# Revit family: QF_BOURGEAT_Satellite4GT_froid_2-1_porte_pleine
name_source: partatom
category: Equipement spécialisé
revit_build: Autodesk Revit 2015 (Build: 20140606_1530(x64)
units: mm (PartAtom-declared; Revit-internal decimal feet)

## types (2) — shared parameters
Certification = NF hygiene alimentaire
Charge max = 300.00 kg
Charge_gaz = 0.220 Kg
Classe Climatique = 4
Consommation énergétique = 4.3Kw/h NFD40-016
Diametre_roue = 160 mm  [stored 0.524934 ft]
Fabricant = BOURGEAT
Fréquence = 50 Hz
Hauteur hors tout = 1876 mm
Hauteur_poignee_porte_sol = 816 mm
Hauteur_poignees_laterales = 905 mm  [stored 2.96916 ft]
Hauteur_porte = 1629 mm  [stored 5.34449 ft]
Hauteur_roue = 200 mm  [stored 0.656168 ft]
Indice de protection = IP25
Intensité nominale = 2 A
Largeur_porte = 706 mm  [stored 2.31627 ft]
Longueur hors tout = 791 mm
Longueur_poignees_laterales = 973 mm  [stored 3.19226 ft]
Materiau_Poignee_porte = B_Elastomère_TPE_S
Materiau_bac = B_Elastomère_TPE_S
Materiau_bandage = B_Elastomère_TPE_S
Materiau_porte = Acier inoxydable, brossé
Materiau_vitre = Verre, vitrage transparent, trempé
Nature isolant = Mousse sans PU
Phase = 2
Poids net à vide = 160.00 kg
Pos_V_IHM = 197 mm
Profondeur hors tout = 1129 mm  [stored 3.70407 ft]
Puissance frigorifique = 465 W à -5°C
Puissance électrique  = 500 W
Spécification du Fabricant = Satellite 4GT
Tension = 230 V
Type Fluide Frigorigène = R134a
URL catalogue = http://www.bourgeat.fr

## per-type parameters (varying)
| type | Modèle | Poignee_droite | Poignee_gauche |
| GN40_porte_inox_tirant_droit | 842540 + 844000 | Oui | Non |
| GN40_porte_inox_tirant_gauche | 842540 | Non | Oui |

note: [stored X ft] marks values corroborated as IEEE doubles in the binary element streams (Revit-internal decimal feet)
